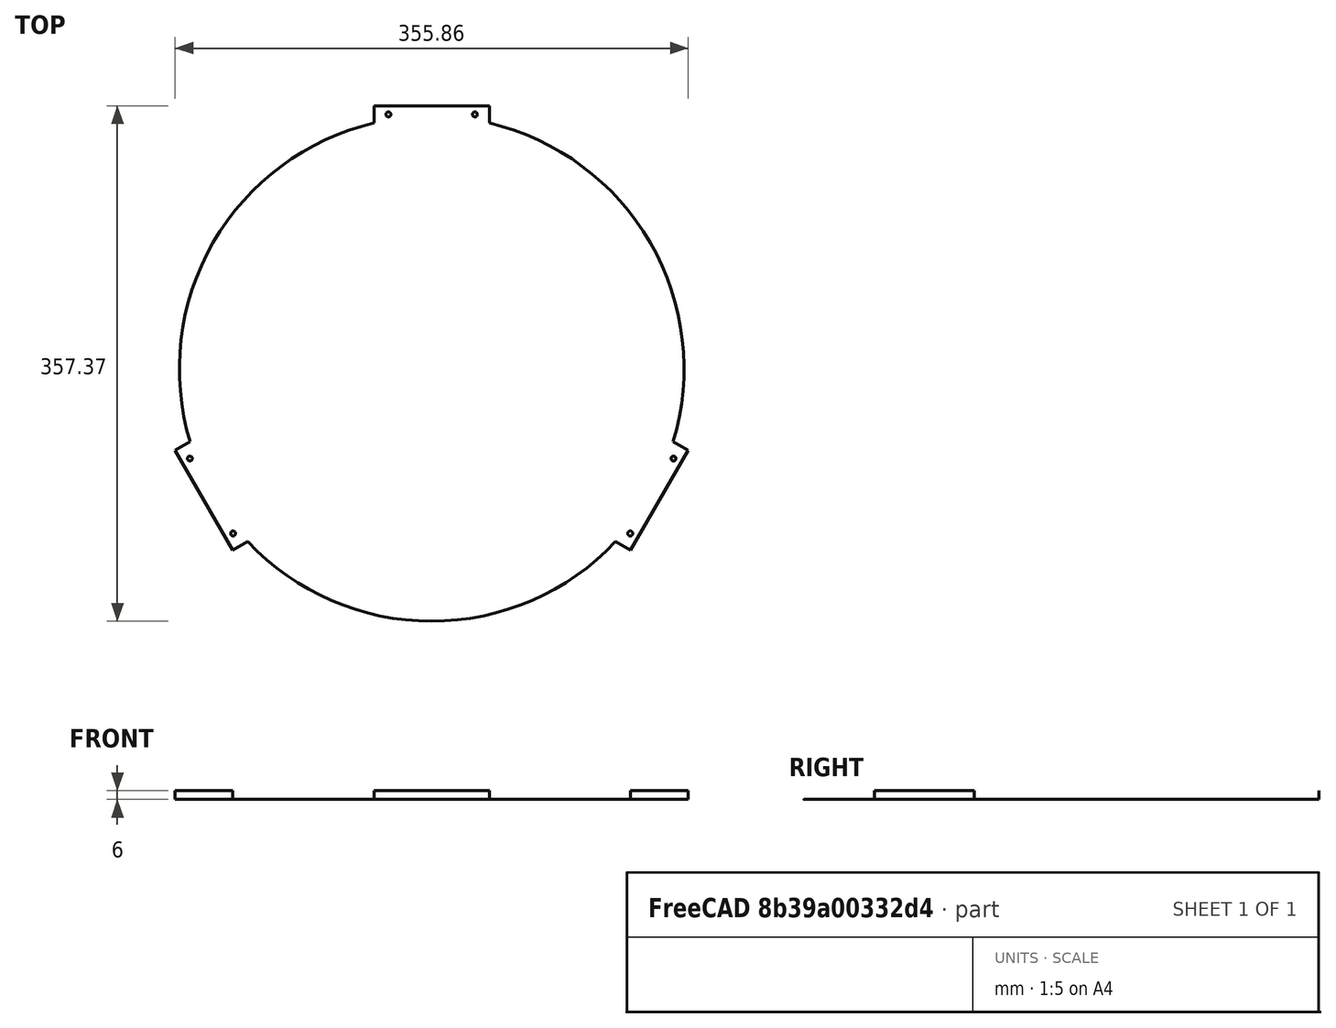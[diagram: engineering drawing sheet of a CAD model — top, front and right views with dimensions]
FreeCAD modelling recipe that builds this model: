
FCSTD DOCUMENT  (FreeCAD 2022.430R26244 +4758 (Git))
Label: As3bed
License: All rights reserved
LicenseURL: http://en.wikipedia.org/wiki/All_rights_reserved
objects: Part::FeaturePython×12, App::FeaturePython×2, App::Link×1
note: 11 computed .brp shape members not serialized (recipe doc carries the construction recipe); baked Part::Feature solids carry a one-line shape summary decoded from their .brp
EXTERNAL_REF file=Bed.FCStd obj=Bed

FEATURE [App::FeaturePython] Constraints  # WARN: FeaturePython — macro-defined, semantics opaque (R4)
  TreeRank = 0
  _LinkVersion = 1
  _Version = 1
FEATURE [App::Link] Link  label="Bed"
  AutoLinkLabel = false
  AutoPlacement = true
  LinkedObject = -> <external Bed.FCStd>#Bed
  SyncGroupVisibility = false
  TreeRank = 0
  _LinkOwner = 131
  _LinkVersion = 1
FEATURE [Part::FeaturePython] Parts  # WARN: FeaturePython — macro-defined, semantics opaque (R4)
  Group = -> [Link]
  GroupMode = 0
  TreeRank = 0
  _LinkVersion = 1
FEATURE [Part::FeaturePython] Assembly  label="As3Bed"  # WARN: FeaturePython — macro-defined, semantics opaque (R4)
  AutoRelax = true
  BuildShape = 0
  Freeze = false
  Group = -> [Constraints,Elements,Parts]
  TreeRank = 0
  Verbose = false
  _LinkVersion = 1
  _SolverType = 1
  _Version = 1
FEATURE [App::FeaturePython] Elements  # WARN: FeaturePython — macro-defined, semantics opaque (R4)
  Group = -> [Element,Element001,Element002,Element004,Element003,Element005,Element006,Element007,Element008,Element009]
  TreeRank = 0
  _LinkVersion = 1
FEATURE [Part::FeaturePython] Element  label="Fix1"  # link proxy (typed FeaturePython)
  Detach = false
  LinkTransform = true
  LinkedObject = -> Link [PolarPattern.Edge23]
  TreeRank = 0
  _LinkVersion = 1
  _Parent = -> Elements
FEATURE [Part::FeaturePython] Element001  label="Fix2"  # link proxy (typed FeaturePython)
  Detach = false
  LinkTransform = true
  LinkedObject = -> Link [PolarPattern.Edge20]
  TreeRank = 0
  _LinkVersion = 1
  _Parent = -> Elements
FEATURE [Part::FeaturePython] Element002  label="Fix3"  # link proxy (typed FeaturePython)
  Detach = false
  LinkTransform = true
  LinkedObject = -> Link [PolarPattern.Edge21]
  TreeRank = 0
  _LinkVersion = 1
  _Parent = -> Elements
FEATURE [Part::FeaturePython] Element003  label="Fix5"  # link proxy (typed FeaturePython)
  Detach = false
  LinkTransform = true
  LinkedObject = -> Link [PolarPattern.Edge24]
  TreeRank = 0
  _LinkVersion = 1
  _Parent = -> Elements
FEATURE [Part::FeaturePython] Element004  label="Fix4"  # link proxy (typed FeaturePython)
  Detach = false
  LinkTransform = true
  LinkedObject = -> Link [PolarPattern.Edge25]
  TreeRank = 0
  _LinkVersion = 1
  _Parent = -> Elements
FEATURE [Part::FeaturePython] Element005  label="Fix6"  # link proxy (typed FeaturePython)
  Detach = false
  LinkTransform = true
  LinkedObject = -> Link [PolarPattern.Edge22]
  TreeRank = 0
  _LinkVersion = 1
  _Parent = -> Elements
FEATURE [Part::FeaturePython] Element006  # link proxy (typed FeaturePython)
  Detach = false
  LinkTransform = true
  LinkedObject = -> Link [PolarPattern.Face4]
  TreeRank = 0
  _LinkVersion = 1
  _Parent = -> Elements
FEATURE [Part::FeaturePython] Element007  # link proxy (typed FeaturePython)
  Detach = false
  LinkTransform = true
  LinkedObject = -> Link [PolarPattern.Face26]
  TreeRank = 0
  _LinkVersion = 1
  _Parent = -> Elements
FEATURE [Part::FeaturePython] Element008  # link proxy (typed FeaturePython)
  Detach = false
  LinkTransform = true
  LinkedObject = -> Link [PolarPattern.Face25]
  TreeRank = 0
  _LinkVersion = 1
  _Parent = -> Elements
FEATURE [Part::FeaturePython] Element009  # link proxy (typed FeaturePython)
  Detach = false
  LinkTransform = true
  LinkedObject = -> Link [PolarPattern.Face24]
  TreeRank = 0
  _LinkVersion = 1
  _Parent = -> Elements
